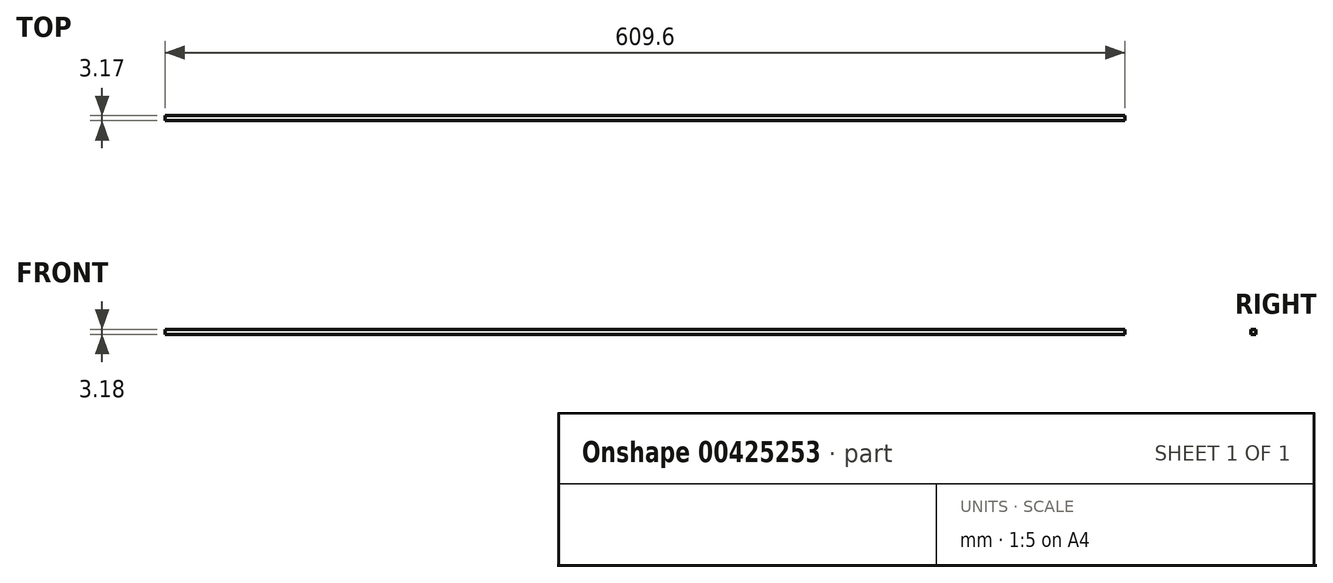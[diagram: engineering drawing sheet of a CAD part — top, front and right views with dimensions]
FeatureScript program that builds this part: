
annotation { "Feature Type Name" : "Feature", "Feature Type Description" : "" }
export const myFeature = defineFeature(function(context is Context, id is Id, definition is map)
    precondition{}
    {
        {
            var Q0;
            Q0=qCreatedBy(makeId("Front.planeOp"),FACE);
            var sketch = newSketch(context, id + "F0", { "sketchPlane" : qUnion([Q0])});
            skLineSegment(sketch, "E0.bottom", {"start": v(-51, 49.38) * mm, "end": v(558.6, 49.38) * mm});
            skLineSegment(sketch, "E0.top", {"start": v(-51, 46.2) * mm, "end": v(558.6, 46.2) * mm});
            skLineSegment(sketch, "E0.left", {"start": v(-51, 49.38) * mm, "end": v(-51, 46.2) * mm});
            skLineSegment(sketch, "E0.right", {"start": v(558.6, 49.38) * mm, "end": v(558.6, 46.2) * mm});
            skSolve(sketch);
        }
        {
            var Q0;
            Q0 = qSketchRegion(id + "F0", true);
            extrude(context, id + "F1", {"entities" : qUnion([Q0]), "depth" : 3.17 * mm});
        }
    });
